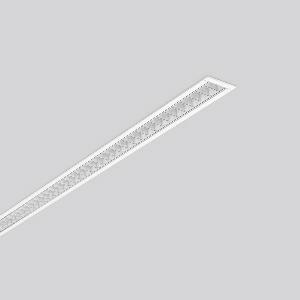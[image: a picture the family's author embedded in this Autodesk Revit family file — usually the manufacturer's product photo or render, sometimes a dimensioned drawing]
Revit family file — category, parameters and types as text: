
# Revit family: less_is_more_27_312179_002_1_76_6609
name_source: partatom
category: Lighting Fixtures
units: mm (PartAtom-declared; Revit-internal decimal feet)

## family parameters
Cut with Voids When Loaded = No
Host = Face
Light Source = No
Part Type = Normal
Room Calculation Point = No
Round Connector Dimension = Use Diameter
Shared = No

## types (1)
- LESS IS MORE 27 (1 x LED Modul 840, 3500 lm, 4000)
    Apparent Load = 39 VA
    CIE Flux Codes = 90 99 100 100 100
    Color Rendering = 80
    Color Temperature = 4000
    Default Elevation = 1800 mm
    Description = Series: LESS IS MORE 27
Recessed ceiling and wall luminaire with slim design. Housing: extruded aluminium profile, powder-coated. End cap aluminium powder-coated. High polish aluminium micro grid. Perfect for office areas (RUG < 19) and environments with computer screens in accordance with EN 12464-1. Suitable for Recessed ceiling mounting, wall (recessed). External driver with connecting cable. 
Colour: traffic white, matt (RAL 9016)
Length: 1514 mm
Width: 38 mm
Height: 2 mm
Cut-out length: 1506 mm
Cut-out width: 30 mm
Recess height: 45-60 mm
Luminaire: recess height: 37 mm
Lamp: LED
Socket: without socket
Colour temperature: 4000K
Colour rendering index (CRI): 82
System power: 39 W
Rated luminous flux: 3500 lm
Luminous efficiency: 90 lm/W
Control gear: Voltage converter, DALI dim.
Protection class: II
Type of protection: IP 20
    Height = 0 mm  [stored 0 ft]
    Lamp = 1 x LED Modul 840
    Lamp Light Flux = 3500 lm
    Lamp count = 1
    Length = 1514 mm
    Lifetime = 50000 h
    Luminous efficacy = 90 lm/W
    Manufacturer = RZB
    ModVariant = No
    Model = 312179.002.1.76
    Mounting Place = Ceiling, Wall
    Mounting Type = Recessed
    Number of Poles = 1
    OnlyDefault = Yes
    Power Factor = 1
    Product Name = LESS IS MORE 27
    Product group = Recessed LED linear luminaires
    ProductGroupID = 407
    Protection Class = Protection class II
    Protection Degree = IP 20
    RLX_Detail_Level = 1
    RLX_Emergency_Light_Flux = 0 lm
    RLX_Emergency_Type = 0
    RLX_Emergency_Type_DB = No
    RlxData = <blob elided: 27045 chars, md5=7f4b09a6>
    Socket = socket
    Standby Power = 0 W
    System Light Flux = 3500 lm
    System Power = 39 W
    Type Comments = Product without accessories
    Type Image = 312177.002.jpg
    URL = http://relux.com
    VarID = ---
    Voltage = 230 V
    Voltage Range = 220-240 V
    Weight = 0.00 kg
    Width = 38 mm

note: [stored X ft] marks values corroborated as IEEE doubles in the binary element streams (Revit-internal decimal feet)

## geometry (parser evidence)
native form markers: Blend x4, Sweep x9
no freeform markers — native parametric forms only
